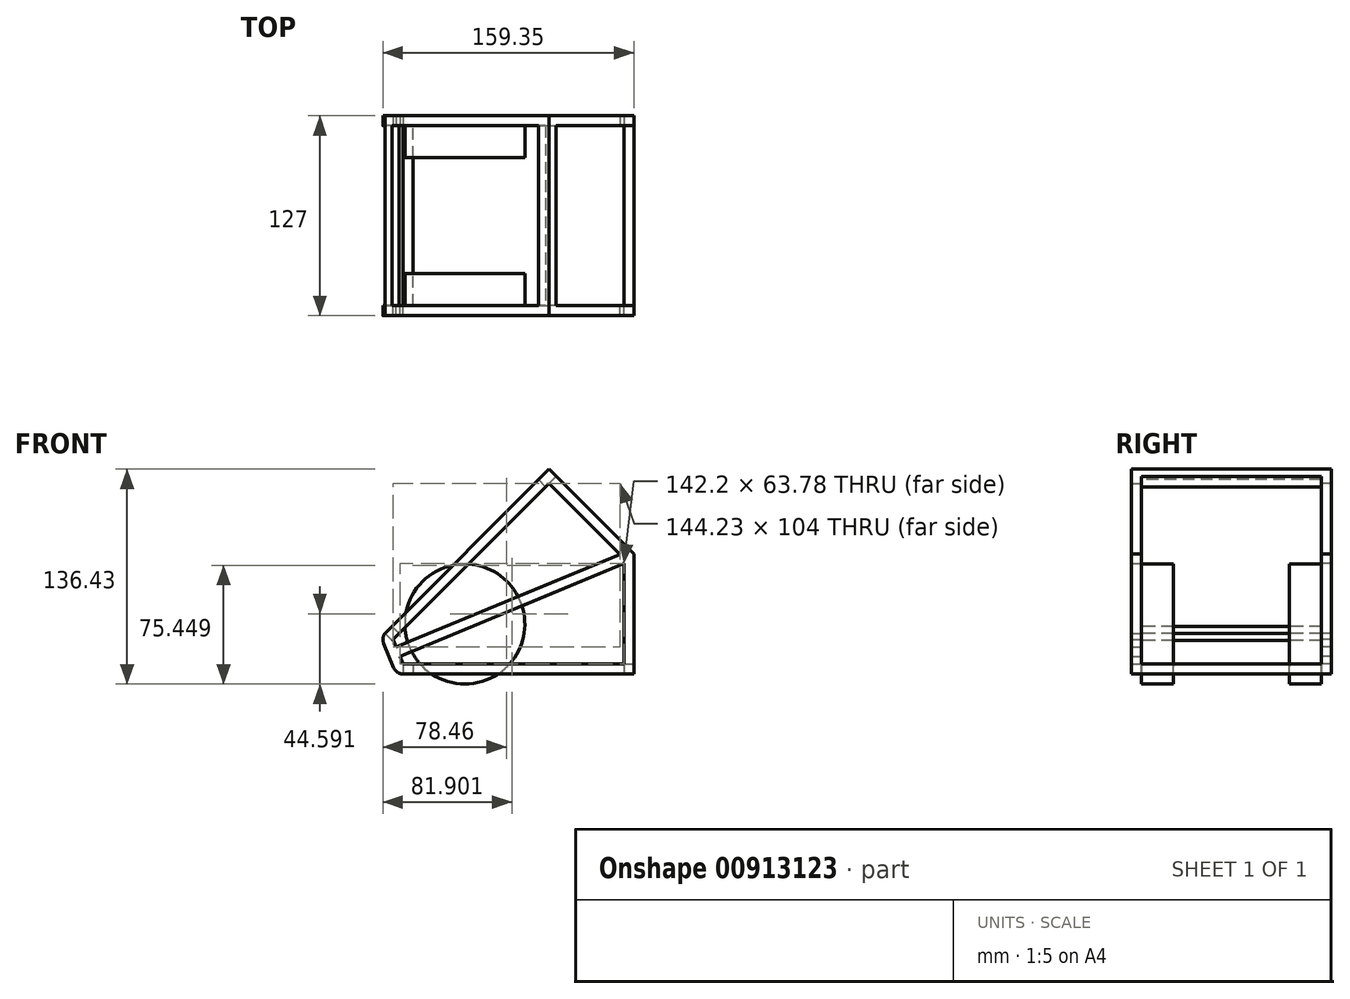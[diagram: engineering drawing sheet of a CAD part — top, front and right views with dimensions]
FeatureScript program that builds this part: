
annotation { "Feature Type Name" : "Feature", "Feature Type Description" : "" }
export const myFeature = defineFeature(function(context is Context, id is Id, definition is map)
    precondition{}
    {
        {
            var Q0;
            Q0=qCreatedBy(makeId("Front.planeOp"),FACE);
            var sketch = newSketch(context, id + "F0", { "sketchPlane" : qUnion([Q0])});
            skLineSegment(sketch, "E0", {"start": v(0, 0) * mm, "end": v(-2.02, 4.88) * mm});
            skLineSegment(sketch, "E1", {"start": v(-6.47, 15.63) * mm, "end": v(92.65, 114.75) * mm});
            skLineSegment(sketch, "E2", {"start": v(92.65, 114.75) * mm, "end": v(137.75, 69.65) * mm});
            skLineSegment(sketch, "E3", {"start": v(140.18, 63.78) * mm, "end": v(140.18, 0) * mm});
            skLineSegment(sketch, "E4", {"start": v(140.18, 0) * mm, "end": v(0, 0) * mm});
            skLineSegment(sketch, "E5.0", {"start": v(146.53, 69.85) * mm, "end": v(146.53, -6.35) * mm});
            skLineSegment(sketch, "E5.1", {"start": v(92.65, 123.73) * mm, "end": v(146.53, 69.85) * mm});
            skLineSegment(sketch, "E5.2", {"start": v(146.53, -6.35) * mm, "end": v(0, -6.35) * mm});
            skLineSegment(sketch, "E5.3", {"start": v(-5.87, -2.43) * mm, "end": v(-12.34, 13.2) * mm});
            skLineSegment(sketch, "E5.4", {"start": v(-10.96, 20.12) * mm, "end": v(92.65, 123.73) * mm});
            skLineSegment(sketch, "E6.0", {"start": v(-4.45, 10.75) * mm, "end": v(137.75, 69.65) * mm});
            skLineSegment(sketch, "E7.0", {"start": v(-2.02, 4.88) * mm, "end": v(140.18, 63.78) * mm});
            skLineSegment(sketch, "E8.trimOffspring", {"start": v(-4.45, 10.75) * mm, "end": v(-6.47, 15.63) * mm});
            skPoint(sketch, "E9.visualSharp", {"position": v(-13.96, 17.12) * mm});
            skArc(sketch, "E9.filletArc", {"start": v(-10.96, 20.12) * mm, "mid": v(-12.7, 16.87) * mm, "end": v(-12.34, 13.2) * mm});
            skPoint(sketch, "E10.visualSharp", {"position": v(-4.24, -6.35) * mm});
            skArc(sketch, "E10.filletArc", {"start": v(-5.87, -2.43) * mm, "mid": v(-3.53, -5.28) * mm, "end": v(0, -6.35) * mm});
            skSolve(sketch);
        }
        {
            var Q0;
            Q0=makeQuery(id+"F0.imprint","IMPRINT",FACE,{"disambiguationData":[TD([[makeQuery(id+"F0.imprint","IMPRINT",EDGE,{"derivedFrom":sQuery(id+"F0.wireOp",EDGE,"E0")}),1.0]])]});
            extrude(context, id + "F1", {"entities" : qUnion([Q0]), "depth" : 6.35 * mm, "offsetDistance" : 25.4 * mm});
        }
        {
            var Q0;
            Q0=qCreatedBy(makeId("Front.planeOp"),FACE);
            cPlane(context, id + "F2", {"entities" : qUnion([Q0]), "cplaneType" : CPlaneType.OFFSET, "offset" : 57.15 * mm, "oppositeDirection" : true, "width" : 152.4 * mm, "height" : 152.4 * mm});
        }
        {
            var Q0;
            Q0=makeQuery(id+"F1.opExtrude","SWEPT_BODY",BODY,{"disambiguationData":[OSD([sQuery(id+"F0.wireOp",EDGE,"E0"),sQuery(id+"F0.wireOp",EDGE,"E1"),sQuery(id+"F0.wireOp",EDGE,"E2"),sQuery(id+"F0.wireOp",EDGE,"E3"),sQuery(id+"F0.wireOp",EDGE,"E4"),sQuery(id+"F0.wireOp",EDGE,"E5.0"),sQuery(id+"F0.wireOp",EDGE,"E5.1"),sQuery(id+"F0.wireOp",EDGE,"E5.2"),sQuery(id+"F0.wireOp",EDGE,"E5.3"),sQuery(id+"F0.wireOp",EDGE,"E5.4"),sQuery(id+"F0.wireOp",EDGE,"E6.0"),sQuery(id+"F0.wireOp",EDGE,"E7.0"),sQuery(id+"F0.wireOp",EDGE,"E8.trimOffspring"),sQuery(id+"F0.wireOp",EDGE,"E9.filletArc"),sQuery(id+"F0.wireOp",EDGE,"E10.filletArc")])]});
            var Q1;
            Q1=qCreatedBy(id+"F2.planeOp",FACE);
            mirror(context, id + "F3", {"entities" : qUnion([Q0]), "mirrorPlane" : qUnion([Q1])});
        }
        {
            var Q0;
            Q0=makeQuery(id+"F3.opPattern","COPY",FACE,{"derivedFrom":makeQuery(id+"F1.opExtrude","SWEPT_FACE",FACE,{"disambiguationData":[OSD([sQuery(id+"F0.wireOp",EDGE,"E5.4")])]}),"instanceName":"1"});
            var sketch = newSketch(context, id + "F4", { "sketchPlane" : qUnion([Q0])});
            skLineSegment(sketch, "E11.bottom", {"start": v(-120.65, 153) * mm, "end": v(6.35, 153) * mm});
            skLineSegment(sketch, "E11.top", {"start": v(-120.65, 5.62) * mm, "end": v(6.35, 5.62) * mm});
            skLineSegment(sketch, "E11.left", {"start": v(-120.65, 153) * mm, "end": v(-120.65, 5.62) * mm});
            skLineSegment(sketch, "E11.right", {"start": v(6.35, 153) * mm, "end": v(6.35, 5.62) * mm});
            skLineSegment(sketch, "E12.bottom", {"start": v(-114.3, 143.62) * mm, "end": v(0, 143.62) * mm});
            skLineSegment(sketch, "E12.top", {"start": v(-114.3, 11.97) * mm, "end": v(0, 11.97) * mm});
            skLineSegment(sketch, "E12.left", {"start": v(-114.3, 143.62) * mm, "end": v(-114.3, 11.97) * mm});
            skLineSegment(sketch, "E12.right", {"start": v(0, 143.62) * mm, "end": v(0, 11.97) * mm});
            skSolve(sketch);
        }
        {
            var Q0;
            Q0 = qSketchRegion(id + "F4", true);
            var Q1;
            {var subQ3=sQuery(id+"F4.wireOp",EDGE,"E11.top");Q1=makeQuery(id+"F4.imprint","IMPRINT",FACE,{"disambiguationData":[TD([[makeQuery(id+"F4.imprint","IMPRINT",EDGE,{"derivedFrom":subQ3}),1.0]])]});}
            extrude(context, id + "F5", {"entities" : qUnion([Q0, Q1]), "operationType" : NewBodyOperationType.ADD, "oppositeDirection" : true, "depth" : 6.35 * mm, "offsetDistance" : 25.4 * mm});
        }
        {
            var Q0;
            Q0=makeQuery(id+"F1.opExtrude","SWEPT_FACE",FACE,{"disambiguationData":[OSD([sQuery(id+"F0.wireOp",EDGE,"E5.2")])]});
            var sketch = newSketch(context, id + "F6", { "sketchPlane" : qUnion([Q0])});
            skLineSegment(sketch, "E13.bottom", {"start": v(0, 6.35) * mm, "end": v(146.53, 6.35) * mm});
            skLineSegment(sketch, "E13.top", {"start": v(0, -120.65) * mm, "end": v(146.53, -120.65) * mm});
            skLineSegment(sketch, "E13.left", {"start": v(0, 6.35) * mm, "end": v(0, -120.65) * mm});
            skLineSegment(sketch, "E13.right", {"start": v(146.53, 6.35) * mm, "end": v(146.53, -120.65) * mm});
            skLineSegment(sketch, "E14.bottom", {"start": v(6.35, 0) * mm, "end": v(140.18, 0) * mm});
            skLineSegment(sketch, "E14.top", {"start": v(6.35, -114.3) * mm, "end": v(140.18, -114.3) * mm});
            skLineSegment(sketch, "E14.left", {"start": v(6.35, 0) * mm, "end": v(6.35, -114.3) * mm});
            skLineSegment(sketch, "E14.right", {"start": v(140.18, 0) * mm, "end": v(140.18, -114.3) * mm});
            skSolve(sketch);
        }
        {
            var Q0;
            Q0 = qSketchRegion(id + "F6", true);
            extrude(context, id + "F7", {"entities" : qUnion([Q0]), "operationType" : NewBodyOperationType.ADD, "oppositeDirection" : true, "depth" : 6.35 * mm, "offsetDistance" : 25.4 * mm});
        }
        {
            var Q0;
            {var subQ0=sQuery(id+"F0.wireOp",EDGE,"E10.filletArc");var subQ3=sQuery(id+"F0.wireOp",EDGE,"E9.filletArc");var subQ5=sQuery(id+"F0.wireOp",EDGE,"E5.3");var subQ7=sQuery(id+"F0.wireOp",EDGE,"E5.2");var subQ10=sQuery(id+"F0.wireOp",EDGE,"E5.0");var subQ16=sQuery(id+"F0.wireOp",EDGE,"E4");var subQ19=sQuery(id+"F0.wireOp",EDGE,"E6.0");var subQ21=sQuery(id+"F0.wireOp",EDGE,"E2");var subQ23=sQuery(id+"F0.wireOp",EDGE,"E1");var subQ24=makeQuery(id+"F1.opExtrude","SWEPT_FACE",FACE,{"disambiguationData":[OSD([subQ23])]});var subQ26=sQuery(id+"F0.wireOp",EDGE,"E7.0");var subQ35=sQuery(id+"F0.wireOp",EDGE,"E5.1");var subQ36=makeQuery(id+"F1.opExtrude","SWEPT_FACE",FACE,{"disambiguationData":[OSD([subQ35])]});var subQ37=sQuery(id+"F0.wireOp",EDGE,"E3");var subQ39=sQuery(id+"F0.wireOp",EDGE,"E0");var subQ42=sQuery(id+"F0.wireOp",EDGE,"E8.trimOffspring");var subQ44=makeQuery(id+"F3.opPattern","COPY",FACE,{"derivedFrom":makeQuery(id+"F1.opExtrude","CAP_FACE",FACE,{"disambiguationData":[OSD([subQ39,subQ23,subQ21,subQ37,subQ16,subQ10,subQ35,subQ7,subQ5,sQuery(id+"F0.wireOp",EDGE,"E5.4"),subQ19,subQ26,subQ42,subQ3,subQ0])],"isStart":true}),"instanceName":"1"});Q0=makeQuery(id+"F7.boolean.opBoolean","SPLIT",FACE,{"disambiguationData":[TD([subQ24])],"derivedFrom":makeQuery(id+"F5.boolean.opBoolean","SPLIT",FACE,{"disambiguationData":[TD([subQ36])],"derivedFrom":subQ44})});}
            var sketch = newSketch(context, id + "F8", { "sketchPlane" : qUnion([Q0])});
            skCircle(sketch, "E15", {"center": v(39.22, 25.4) * mm, "radius": 38.1 * mm});
            skSolve(sketch);
        }
        {
            var Q0;
            Q0 = qSketchRegion(id + "F8", true);
            extrude(context, id + "F9", {"entities" : qUnion([Q0]), "depth" : 20.32 * mm, "offsetDistance" : 25.4 * mm});
        }
        {
            var Q0;
            Q0=makeQuery(id+"F9.opExtrude","SWEPT_BODY",BODY,{"disambiguationData":[OSD([sQuery(id+"F8.wireOp",EDGE,"E15")])]});
            var Q1;
            Q1=qCreatedBy(id+"F2.planeOp",FACE);
            mirror(context, id + "F10", {"operationType" : NewBodyOperationType.ADD, "entities" : qUnion([Q0]), "mirrorPlane" : qUnion([Q1])});
        }
    });
